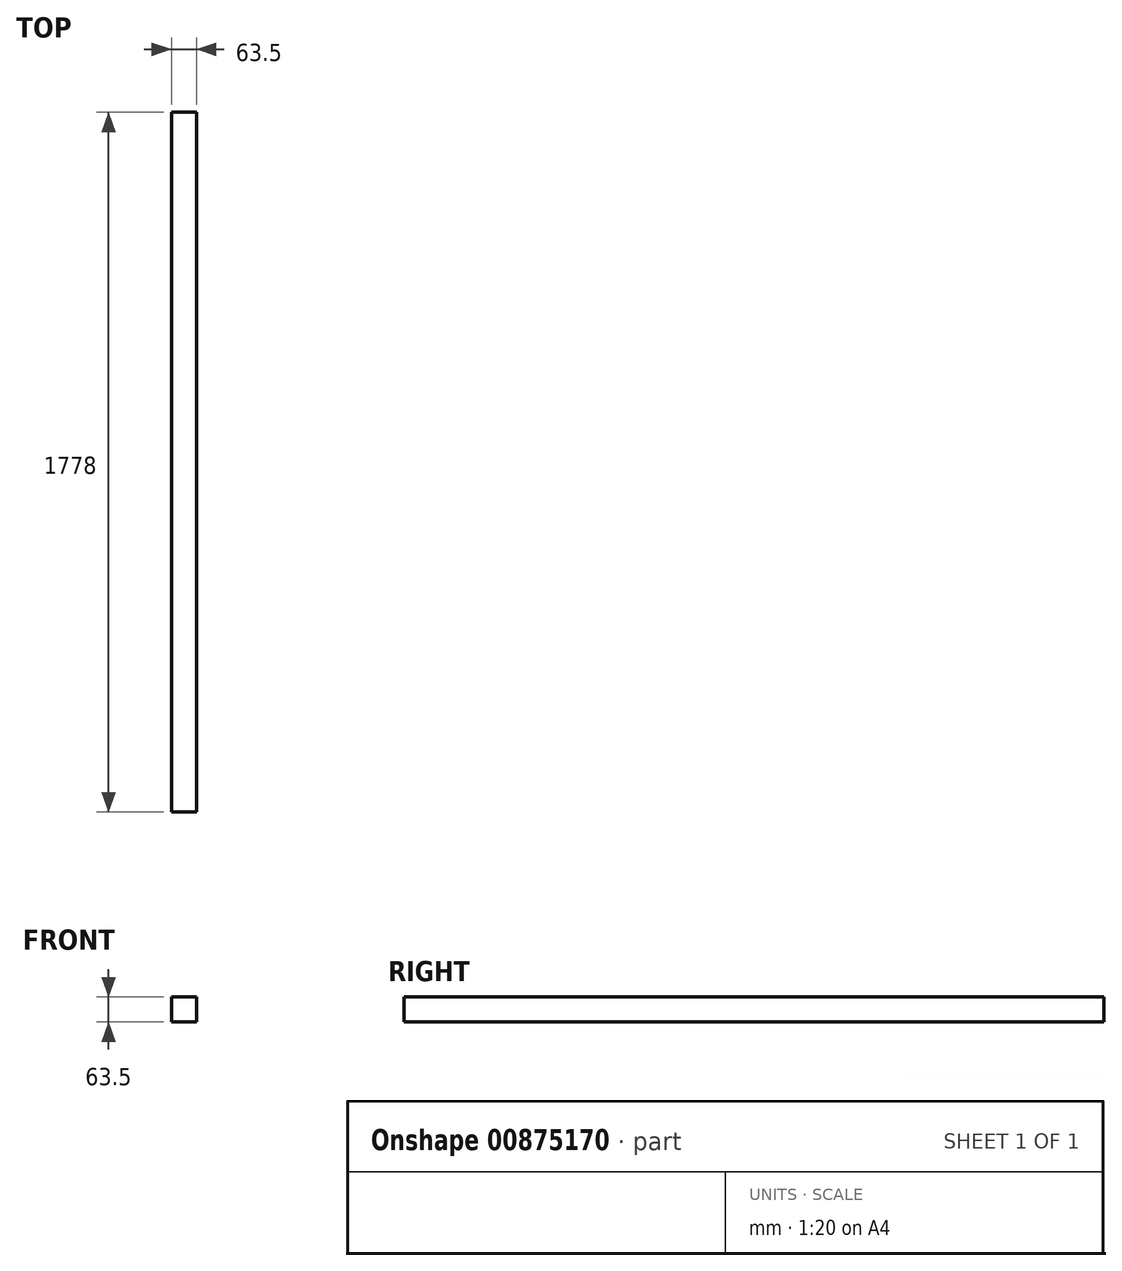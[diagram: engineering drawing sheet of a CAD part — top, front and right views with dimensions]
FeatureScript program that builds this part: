
annotation { "Feature Type Name" : "Feature", "Feature Type Description" : "" }
export const myFeature = defineFeature(function(context is Context, id is Id, definition is map)
    precondition{}
    {
        {
            var Q0;
            Q0=qCreatedBy(makeId("Front.planeOp"),FACE);
            var sketch = newSketch(context, id + "F0", { "sketchPlane" : qUnion([Q0])});
            skLineSegment(sketch, "E0.bottom", {"start": v(-164.57, 68.12) * mm, "end": v(-101.07, 68.12) * mm});
            skLineSegment(sketch, "E0.top", {"start": v(-164.57, 4.62) * mm, "end": v(-101.07, 4.62) * mm});
            skLineSegment(sketch, "E0.left", {"start": v(-164.57, 68.12) * mm, "end": v(-164.57, 4.62) * mm});
            skLineSegment(sketch, "E0.right", {"start": v(-101.07, 68.12) * mm, "end": v(-101.07, 4.62) * mm});
            skSolve(sketch);
        }
        {
            var Q0;
            Q0=makeQuery(id+"F0.imprint","IMPRINT",FACE,{"disambiguationData":[TD([[makeQuery(id+"F0.imprint","IMPRINT",EDGE,{"derivedFrom":sQuery(id+"F0.wireOp",EDGE,"E0.bottom")}),-1.0]])]});
            extrude(context, id + "F1", {"entities" : qUnion([Q0]), "depth" : 1498.6 * mm, "offsetDistance" : 25.4 * mm});
        }
        {
            var Q0;
            Q0=makeQuery(id+"F1.opExtrude","CAP_FACE",FACE,{"disambiguationData":[OSD([sQuery(id+"F0.wireOp",EDGE,"E0.bottom"),sQuery(id+"F0.wireOp",EDGE,"E0.top"),sQuery(id+"F0.wireOp",EDGE,"E0.left"),sQuery(id+"F0.wireOp",EDGE,"E0.right")])],"isStart":true});
            extrude(context, id + "F2", {"entities" : qUnion([Q0]), "operationType" : NewBodyOperationType.REMOVE, "oppositeDirection" : true, "depth" : 1092.2 * mm, "offsetDistance" : 25.4 * mm});
        }
        {
            var Q0;
            Q0=makeQuery(id+"F2.boolean.opBoolean","COPY",FACE,{"derivedFrom":makeQuery(id+"F2.opExtrude","CAP_FACE",FACE,{"disambiguationData":[OSD([sQuery(id+"F0.wireOp",EDGE,"E0.bottom"),sQuery(id+"F0.wireOp",EDGE,"E0.top"),sQuery(id+"F0.wireOp",EDGE,"E0.left"),sQuery(id+"F0.wireOp",EDGE,"E0.right")])],"isStart":false})});
            extrude(context, id + "F3", {"entities" : qUnion([Q0]), "operationType" : NewBodyOperationType.REMOVE, "oppositeDirection" : true, "depth" : 203.2 * mm, "offsetDistance" : 25.4 * mm});
        }
        {
            var Q0;
            Q0=makeQuery(id+"F1.opExtrude","CAP_FACE",FACE,{"disambiguationData":[OSD([sQuery(id+"F0.wireOp",EDGE,"E0.bottom"),sQuery(id+"F0.wireOp",EDGE,"E0.top"),sQuery(id+"F0.wireOp",EDGE,"E0.left"),sQuery(id+"F0.wireOp",EDGE,"E0.right")])],"isStart":false});
            extrude(context, id + "F4", {"entities" : qUnion([Q0]), "operationType" : NewBodyOperationType.REMOVE, "oppositeDirection" : true, "depth" : 177.8 * mm, "offsetDistance" : 25.4 * mm});
        }
        {
            var Q0;
            Q0=makeQuery(id+"F3.boolean.opBoolean","COPY",FACE,{"derivedFrom":makeQuery(id+"F3.opExtrude","CAP_FACE",FACE,{"disambiguationData":[OSD([sQuery(id+"F0.wireOp",EDGE,"E0.bottom"),sQuery(id+"F0.wireOp",EDGE,"E0.top"),sQuery(id+"F0.wireOp",EDGE,"E0.left"),sQuery(id+"F0.wireOp",EDGE,"E0.right")])],"isStart":false})});
            extrude(context, id + "F5", {"entities" : qUnion([Q0]), "operationType" : NewBodyOperationType.ADD, "depth" : 1117.6 * mm, "offsetDistance" : 25.4 * mm});
        }
        {
            var Q0;
            Q0=makeQuery(id+"F5.opExtrude","CAP_FACE",FACE,{"disambiguationData":[OSD([sQuery(id+"F0.wireOp",EDGE,"E0.bottom"),sQuery(id+"F0.wireOp",EDGE,"E0.top"),sQuery(id+"F0.wireOp",EDGE,"E0.left"),sQuery(id+"F0.wireOp",EDGE,"E0.right")])],"isStart":false});
            extrude(context, id + "F6", {"entities" : qUnion([Q0]), "operationType" : NewBodyOperationType.ADD, "depth" : 635 * mm, "offsetDistance" : 25.4 * mm});
        }
    });
